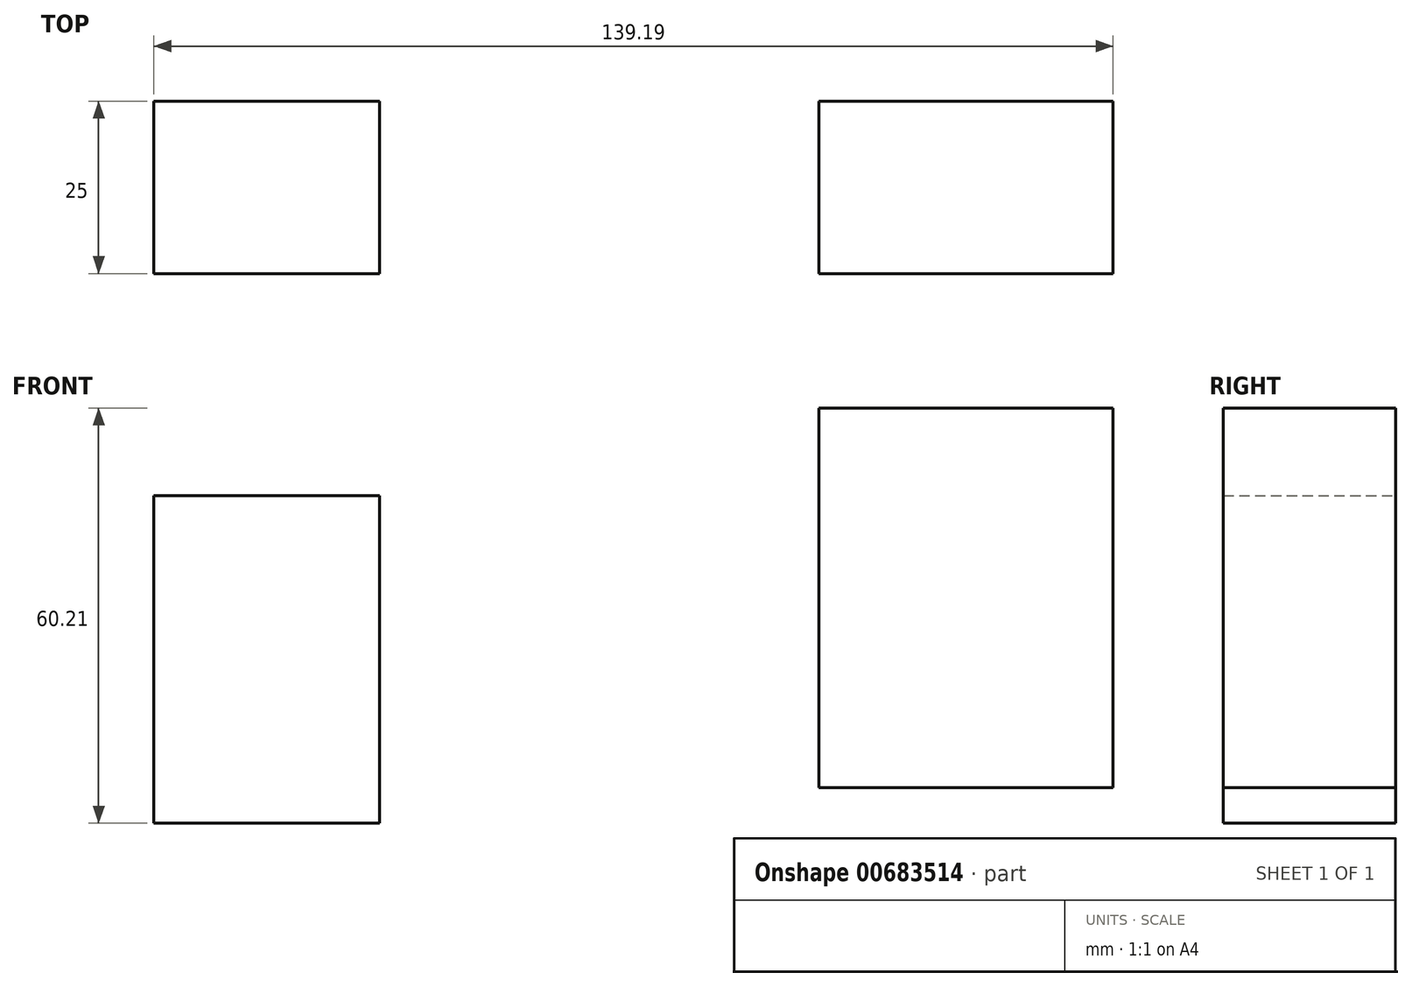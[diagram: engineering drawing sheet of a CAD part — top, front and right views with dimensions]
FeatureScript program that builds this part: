
annotation { "Feature Type Name" : "Feature", "Feature Type Description" : "" }
export const myFeature = defineFeature(function(context is Context, id is Id, definition is map)
    precondition{}
    {
        {
            var Q0;
            Q0=qCreatedBy(makeId("Front.planeOp"),FACE);
            var sketch = newSketch(context, id + "F0", { "sketchPlane" : qUnion([Q0])});
            skLineSegment(sketch, "E0.bottom", {"start": v(-122.67, 12.49) * mm, "end": v(-89.96, 12.49) * mm});
            skLineSegment(sketch, "E0.top", {"start": v(-122.67, 59.98) * mm, "end": v(-89.96, 59.98) * mm});
            skLineSegment(sketch, "E0.left", {"start": v(-122.67, 12.49) * mm, "end": v(-122.67, 59.98) * mm});
            skLineSegment(sketch, "E0.right", {"start": v(-89.96, 12.49) * mm, "end": v(-89.96, 59.98) * mm});
            skPoint(sketch, "E0.middle", {"position": v(-106.31, 36.23) * mm});
            skLineSegment(sketch, "E1.bottom", {"start": v(-26.2, 17.64) * mm, "end": v(16.52, 17.64) * mm});
            skLineSegment(sketch, "E1.top", {"start": v(-26.2, 72.7) * mm, "end": v(16.52, 72.7) * mm});
            skLineSegment(sketch, "E1.left", {"start": v(-26.2, 17.64) * mm, "end": v(-26.2, 72.7) * mm});
            skLineSegment(sketch, "E1.right", {"start": v(16.52, 17.64) * mm, "end": v(16.52, 72.7) * mm});
            skPoint(sketch, "E1.middle", {"position": v(-4.84, 45.17) * mm});
            skSolve(sketch);
        }
        {
            var Q0;
            Q0=makeQuery(id+"F0.imprint","IMPRINT",FACE,{"disambiguationData":[TD([[makeQuery(id+"F0.imprint","IMPRINT",EDGE,{"derivedFrom":sQuery(id+"F0.wireOp",EDGE,"E0.bottom")}),1.0]])]});
            var Q1;
            Q1=makeQuery(id+"F0.imprint","IMPRINT",FACE,{"disambiguationData":[TD([[makeQuery(id+"F0.imprint","IMPRINT",EDGE,{"derivedFrom":sQuery(id+"F0.wireOp",EDGE,"E1.bottom")}),1.0]])]});
            extrude(context, id + "F1", {"entities" : qUnion([Q0, Q1]), "depth" : 25 * mm, "offsetDistance" : 25 * mm});
        }
    });
